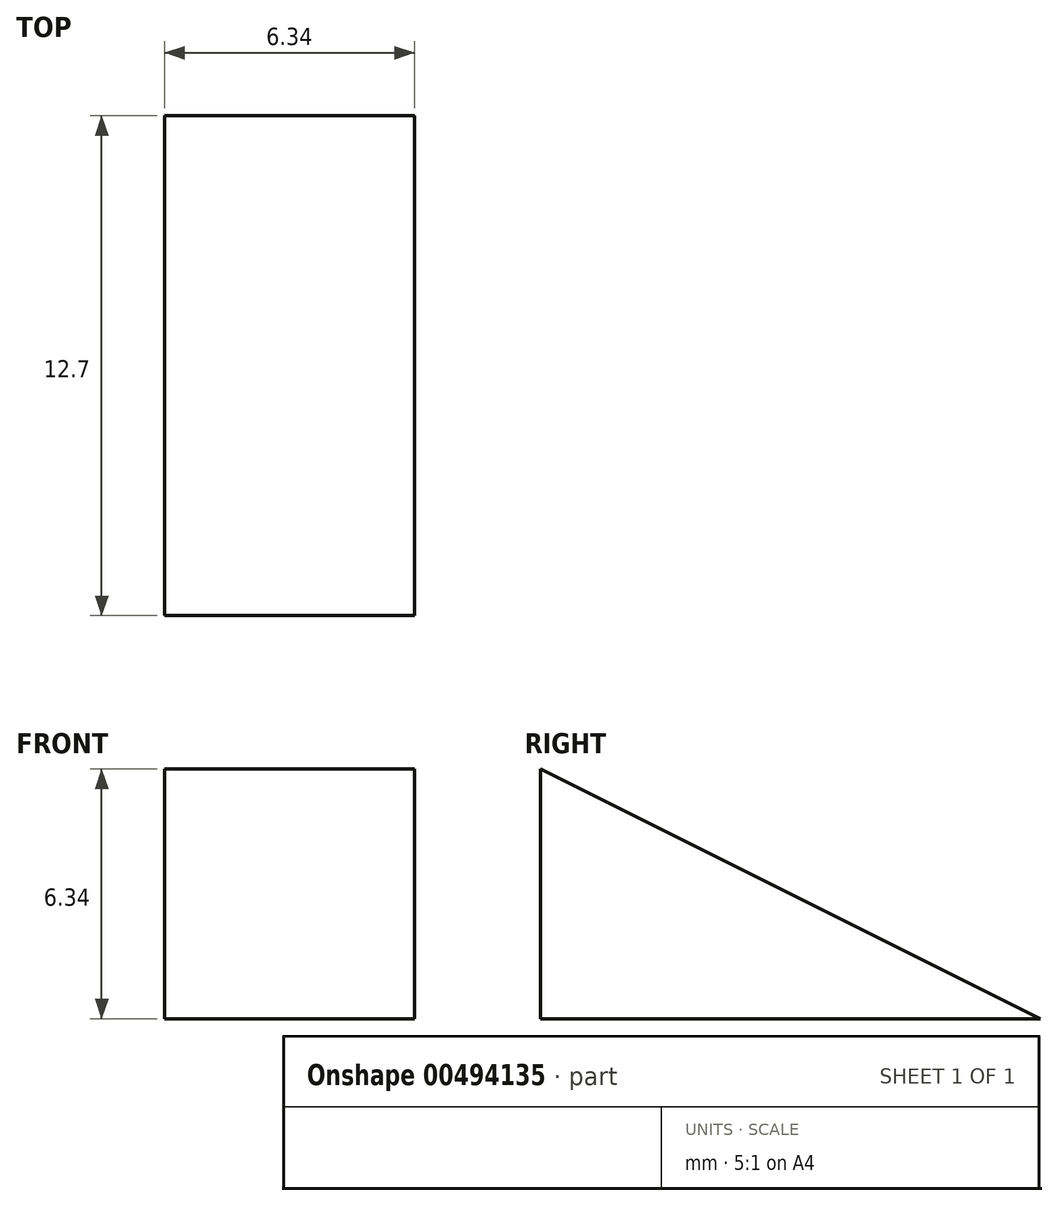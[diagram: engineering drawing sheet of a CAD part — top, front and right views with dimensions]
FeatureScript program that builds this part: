
annotation { "Feature Type Name" : "Feature", "Feature Type Description" : "" }
export const myFeature = defineFeature(function(context is Context, id is Id, definition is map)
    precondition{}
    {
        {
            var Q0;
            Q0=qCreatedBy(makeId("Right.planeOp"),FACE);
            var sketch = newSketch(context, id + "F0", { "sketchPlane" : qUnion([Q0])});
            skLineSegment(sketch, "E0.top", {"start": v(-6.35, -3.18) * mm, "end": v(6.35, -3.18) * mm});
            skLineSegment(sketch, "E0.left", {"start": v(-6.35, 3.18) * mm, "end": v(-6.35, -3.18) * mm});
            skPoint(sketch, "E0.middle", {"position": v(0, 0) * mm});
            skLineSegment(sketch, "E1", {"start": v(-6.35, 3.18) * mm, "end": v(6.35, -3.18) * mm});
            skSolve(sketch);
        }
        {
            var Q0;
            Q0=qSketchRegion(id+"F0",true);
            extrude(context, id + "F1", {"entities" : qUnion([Q0]), "endBound" : BoundingType.SYMMETRIC, "depth" : 6.35 * mm});
        }
        {
            var Q0;
            Q0=makeQuery(id+"F1.opExtrude","SWEPT_FACE",FACE,{"disambiguationData":[OSD([sQuery(id+"F0.wireOp",EDGE,"E0.top")])]});
            var sketch = newSketch(context, id + "F2", { "sketchPlane" : qUnion([Q0])});
            skLineSegment(sketch, "E2", {"start": v(3.18, 0) * mm, "end": v(-3.18, 0) * mm});
            skSolve(sketch);
        }
    });
